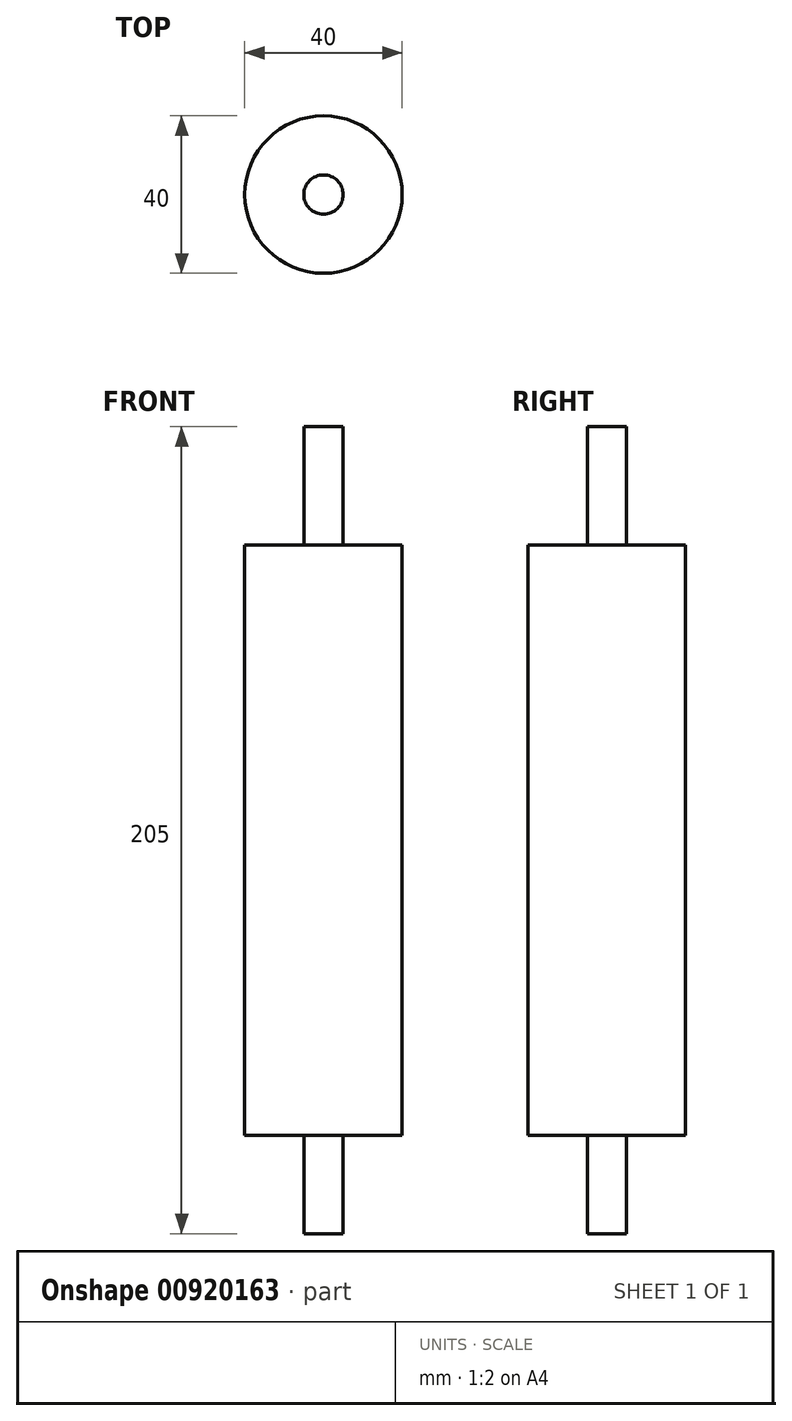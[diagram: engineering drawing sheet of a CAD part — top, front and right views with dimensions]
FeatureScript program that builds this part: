
annotation { "Feature Type Name" : "Feature", "Feature Type Description" : "" }
export const myFeature = defineFeature(function(context is Context, id is Id, definition is map)
    precondition{}
    {
        {
            var Q0;
            Q0=qCreatedBy(makeId("Top.planeOp"),FACE);
            var sketch = newSketch(context, id + "F0", { "sketchPlane" : qUnion([Q0])});
            skCircle(sketch, "E0", {"center": v(0, 0) * mm, "radius": 20 * mm});
            skCircle(sketch, "E1", {"center": v(0, 0) * mm, "radius": 5 * mm});
            skSolve(sketch);
        }
        {
            var Q0;
            Q0=makeQuery(id+"F0.imprint","IMPRINT",FACE,{"disambiguationData":[TD([[makeQuery(id+"F0.imprint","IMPRINT",EDGE,{"derivedFrom":sQuery(id+"F0.wireOp",EDGE,"E0")}),1.0]])]});
            extrude(context, id + "F1", {"entities" : qUnion([Q0]), "depth" : 150 * mm, "offsetDistance" : 25 * mm});
        }
        {
            var Q0;
            Q0=makeQuery(id+"F0.imprint","IMPRINT",FACE,{"disambiguationData":[TD([[makeQuery(id+"F0.imprint","IMPRINT",EDGE,{"derivedFrom":sQuery(id+"F0.wireOp",EDGE,"E1")}),1.0]])]});
            extrude(context, id + "F2", {"entities" : qUnion([Q0]), "operationType" : NewBodyOperationType.ADD, "depth" : 180 * mm, "offsetDistance" : 25 * mm, "hasSecondDirection" : true, "secondDirectionOppositeDirection" : true, "secondDirectionDepth" : 25 * mm});
        }
    });
